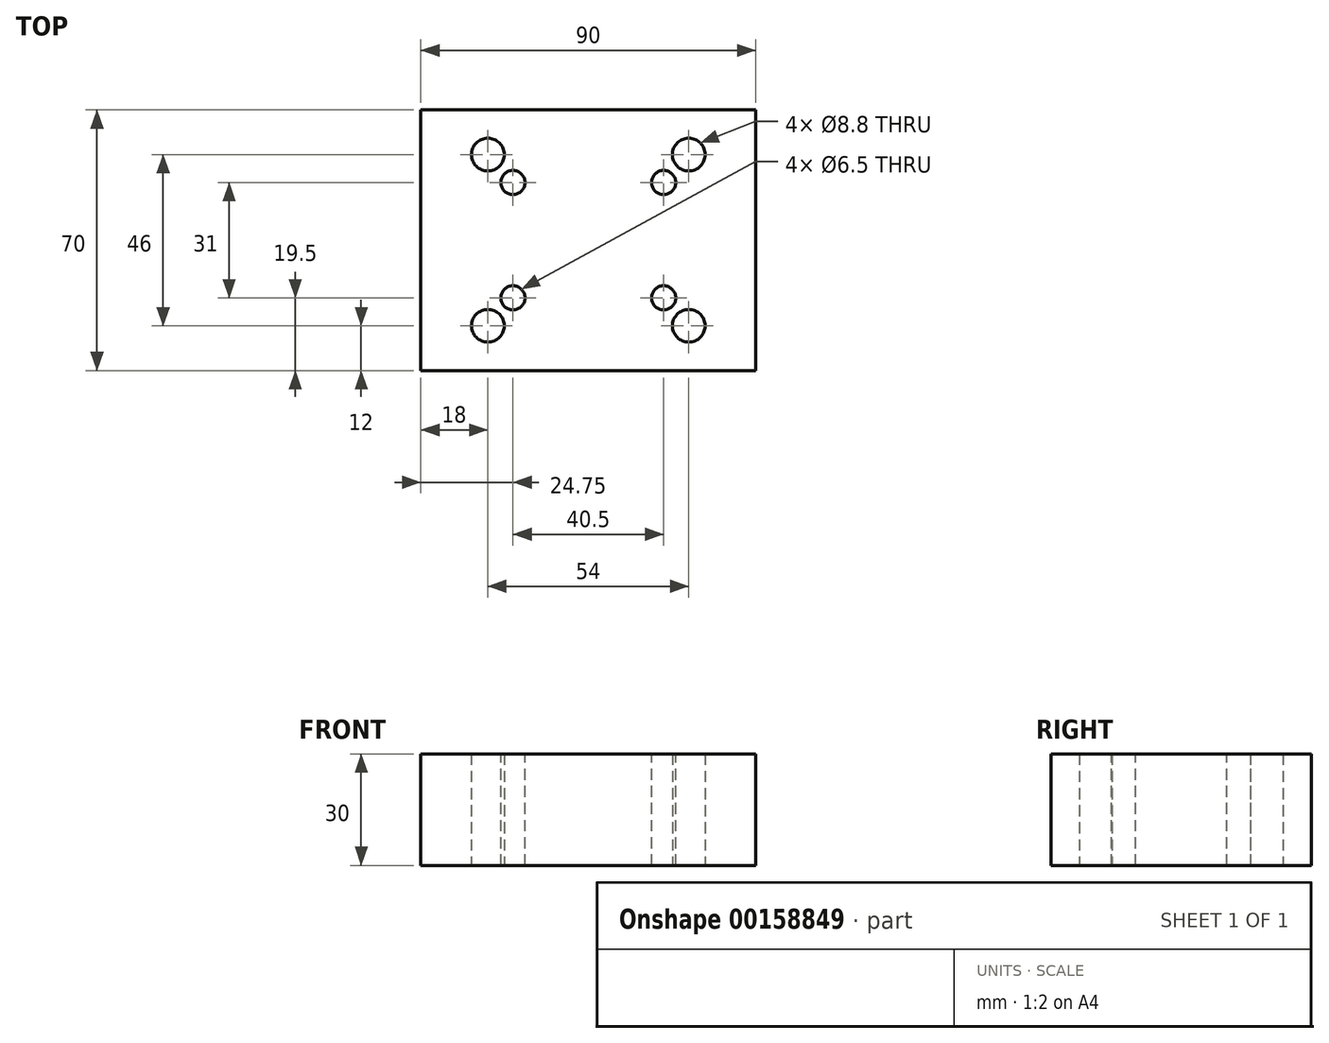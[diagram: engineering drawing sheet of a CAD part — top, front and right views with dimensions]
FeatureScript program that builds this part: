
annotation { "Feature Type Name" : "Feature", "Feature Type Description" : "" }
export const myFeature = defineFeature(function(context is Context, id is Id, definition is map)
    precondition{}
    {
        {
            var Q0;
            Q0=qCreatedBy(makeId("Top.planeOp"),FACE);
            var sketch = newSketch(context, id + "F0", { "sketchPlane" : qUnion([Q0])});
            skLineSegment(sketch, "E0.bottom", {"start": v(-45, -34.19) * mm, "end": v(45, -34.19) * mm});
            skLineSegment(sketch, "E0.top", {"start": v(-45, 35.81) * mm, "end": v(45, 35.81) * mm});
            skLineSegment(sketch, "E0.left", {"start": v(-45, -34.19) * mm, "end": v(-45, 35.81) * mm});
            skLineSegment(sketch, "E0.right", {"start": v(45, -34.19) * mm, "end": v(45, 35.81) * mm});
            skPoint(sketch, "E0.middle", {"position": v(0, 0.81) * mm});
            skPoint(sketch, "E1", {"position": v(-27, 23.81) * mm});
            skPoint(sketch, "E2", {"position": v(-27, -22.19) * mm});
            skPoint(sketch, "E3", {"position": v(27, -22.19) * mm});
            skPoint(sketch, "E4", {"position": v(27, 23.81) * mm});
            skSolve(sketch);
        }
        {
            var Q0;
            Q0=qSketchRegion(id+"F0",true);
            extrude(context, id + "F1", {"entities" : qUnion([Q0]), "depth" : 30 * mm});
        }
        {
            var Q0;
            Q0=sQuery(id+"F0.wireOp",VERTEX,"E1");
            var Q1;
            Q1=sQuery(id+"F0.wireOp",VERTEX,"E2");
            var Q2;
            Q2=sQuery(id+"F0.wireOp",VERTEX,"E3");
            var Q3;
            Q3=sQuery(id+"F0.wireOp",VERTEX,"E4");
            var Q4;
            Q4=makeQuery(id+"F1.opExtrude","SWEPT_BODY",BODY,{"disambiguationData":[OSD([sQuery(id+"F0.wireOp",EDGE,"E0.bottom"),sQuery(id+"F0.wireOp",EDGE,"E0.top"),sQuery(id+"F0.wireOp",EDGE,"E0.left"),sQuery(id+"F0.wireOp",EDGE,"E0.right")])]});
            hole(context, id + "F2", {"style" : HoleStyle.SIMPLE, "endStyle" : HoleEndStyle.THROUGH, "oppositeDirection" : true, "standardTappedOrClearance" : lookupTablePath({ "standard" : "ISO", "engagement" : "75%", "pitch" : "1.25 mm", "size" : "M10", "type" : "Tapped" }), "standardBlindInLast" : lookupTablePath({ "standard" : "ISO", "engagement" : "75%", "pitch" : "1.25 mm", "size" : "M10", "type" : "Tapped" }), "holeDiameter" : 8.8 * mm, "locations" : qUnion([Q0, Q1, Q2, Q3]), "scope" : qUnion([Q4]), "isTappedThrough" : true, "majorDiameter" : 10 * mm, "showTappedDepth" : true});
        }
        {
            var Q0;
            Q0=makeQuery(id+"F1.opExtrude","CAP_FACE",FACE,{"disambiguationData":[OSD([sQuery(id+"F0.wireOp",EDGE,"E0.bottom"),sQuery(id+"F0.wireOp",EDGE,"E0.top"),sQuery(id+"F0.wireOp",EDGE,"E0.left"),sQuery(id+"F0.wireOp",EDGE,"E0.right")])],"isStart":false});
            var sketch = newSketch(context, id + "F3", { "sketchPlane" : qUnion([Q0])});
            skPoint(sketch, "E5", {"position": v(-20.25, 16.31) * mm});
            skPoint(sketch, "E6", {"position": v(20.25, 16.31) * mm});
            skPoint(sketch, "E7", {"position": v(20.25, -14.69) * mm});
            skPoint(sketch, "E8", {"position": v(-20.25, -14.69) * mm});
            skSolve(sketch);
        }
        {
            var Q0;
            Q0=sQuery(id+"F3.wireOp",VERTEX,"E5");
            var Q1;
            Q1=sQuery(id+"F3.wireOp",VERTEX,"E8");
            var Q2;
            Q2=sQuery(id+"F3.wireOp",VERTEX,"E7");
            var Q3;
            Q3=sQuery(id+"F3.wireOp",VERTEX,"E6");
            var Q4;
            Q4=makeQuery(id+"F1.opExtrude","SWEPT_BODY",BODY,{"disambiguationData":[OSD([sQuery(id+"F0.wireOp",EDGE,"E0.bottom"),sQuery(id+"F0.wireOp",EDGE,"E0.top"),sQuery(id+"F0.wireOp",EDGE,"E0.left"),sQuery(id+"F0.wireOp",EDGE,"E0.right")])]});
            hole(context, id + "F4", {"style" : HoleStyle.SIMPLE, "endStyle" : HoleEndStyle.THROUGH, "holeDiameter" : 6.5 * mm, "locations" : qUnion([Q0, Q1, Q2, Q3]), "scope" : qUnion([Q4]), "isTappedThrough" : true});
        }
    });
